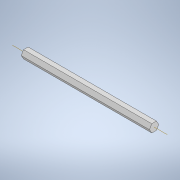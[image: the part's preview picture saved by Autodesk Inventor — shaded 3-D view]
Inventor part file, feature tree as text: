
AUTODESK INVENTOR PART (.ipt)
format: ipt  version: 2021 (Build 250183000, 183)  size: 95,744 bytes
history: native  units: in
note: dims shown in document units (in); Inventor stores cm internally (conversion verified against a paired STEP export)
features: extrude x1, sketch x1
ambient origin geometry x8: Origin, YZ Plane, XZ Plane, XY Plane, X Axis, Y Axis, Z Axis, Center Point
bodies: Solid1 (feature_tree)
feature tree (2):
  extrude  "Extrusion1"  Depth=8.0in TaperAngle=0.0deg
  sketch  "Sketch1"  dims[d0=0.25in d1=8.0in d2=0.0in]
